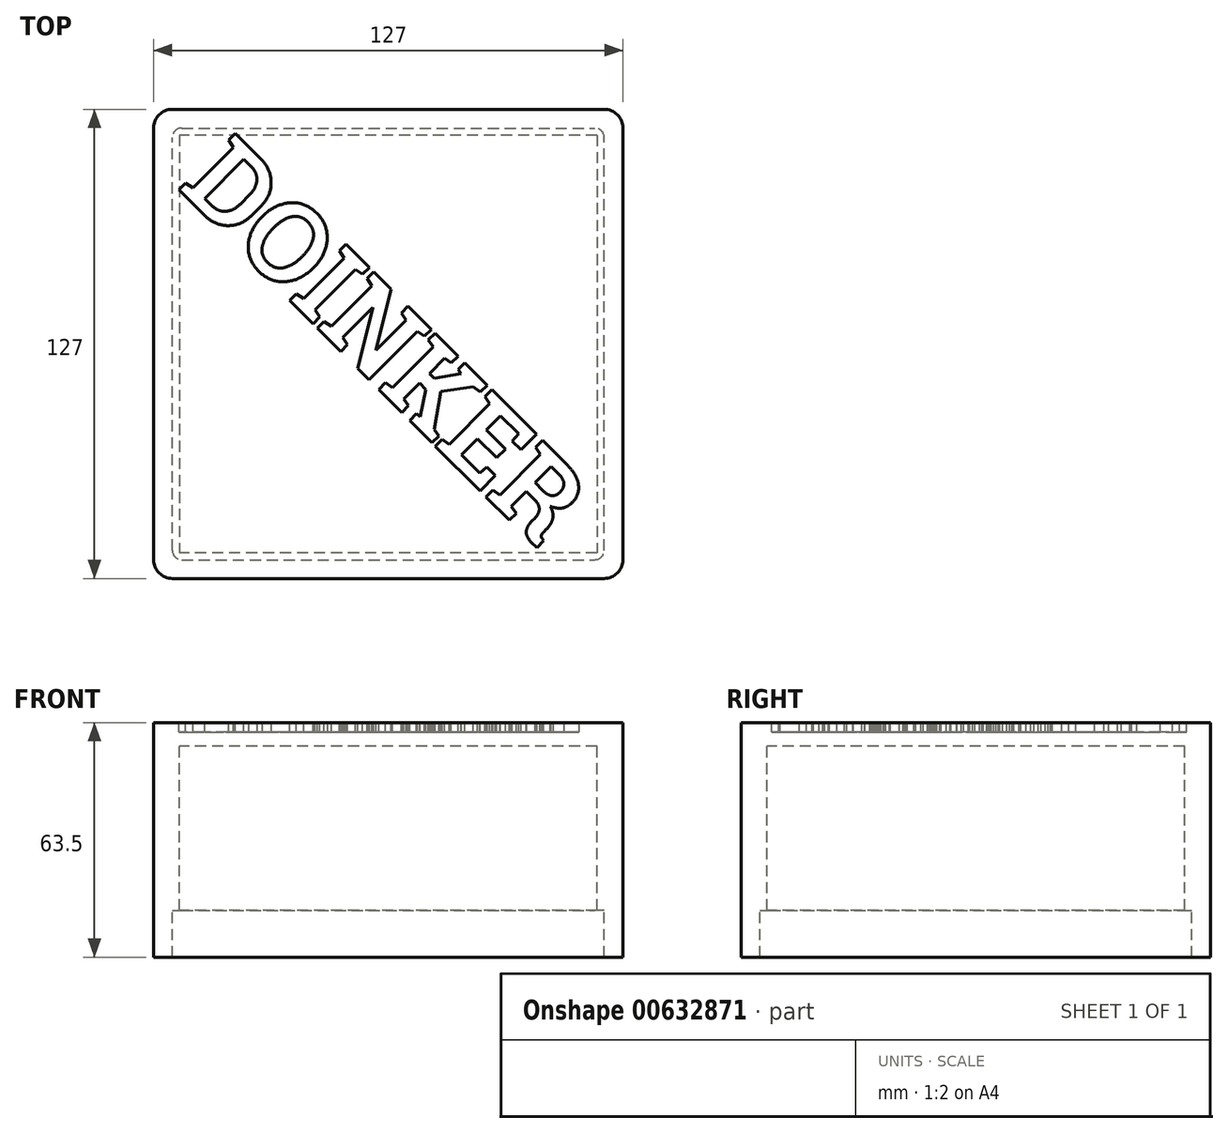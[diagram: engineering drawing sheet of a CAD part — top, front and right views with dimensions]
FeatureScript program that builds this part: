
annotation { "Feature Type Name" : "Feature", "Feature Type Description" : "" }
export const myFeature = defineFeature(function(context is Context, id is Id, definition is map)
    precondition{}
    {
        {
            var Q0;
            Q0=qCreatedBy(makeId("Top.planeOp"),FACE);
            var sketch = newSketch(context, id + "F0", { "sketchPlane" : qUnion([Q0])});
            skLineSegment(sketch, "E0.bottom", {"start": v(56.51, 56.52) * mm, "end": v(-56.52, 56.52) * mm});
            skLineSegment(sketch, "E0.top", {"start": v(56.52, -56.52) * mm, "end": v(-56.51, -56.52) * mm});
            skLineSegment(sketch, "E0.left", {"start": v(56.51, 56.52) * mm, "end": v(56.52, -56.52) * mm});
            skLineSegment(sketch, "E0.right", {"start": v(-56.52, 56.52) * mm, "end": v(-56.51, -56.52) * mm});
            skPoint(sketch, "E0.middle", {"position": v(0, 0) * mm});
            skLineSegment(sketch, "E1.bottom", {"start": v(-63.5, 63.5) * mm, "end": v(63.5, 63.5) * mm});
            skLineSegment(sketch, "E1.top", {"start": v(-63.5, -63.5) * mm, "end": v(63.5, -63.5) * mm});
            skLineSegment(sketch, "E1.left", {"start": v(-63.5, 63.5) * mm, "end": v(-63.5, -63.5) * mm});
            skLineSegment(sketch, "E1.right", {"start": v(63.5, 63.5) * mm, "end": v(63.5, -63.5) * mm});
            skSolve(sketch);
        }
        {
            var Q0;
            Q0=qSketchRegion(id+"F0",true);
            extrude(context, id + "F1", {"entities" : qUnion([Q0]), "oppositeDirection" : true, "depth" : 50.8 * mm, "offsetDistance" : 25.4 * mm});
        }
        {
            var Q0;
            Q0=qCreatedBy(makeId("Top.planeOp"),FACE);
            var sketch = newSketch(context, id + "F2", { "sketchPlane" : qUnion([Q0])});
            skLineSegment(sketch, "E2.bottom", {"start": v(56.51, 56.52) * mm, "end": v(-56.52, 56.52) * mm});
            skLineSegment(sketch, "E2.top", {"start": v(56.52, -56.52) * mm, "end": v(-56.51, -56.52) * mm});
            skLineSegment(sketch, "E2.left", {"start": v(56.51, 56.52) * mm, "end": v(56.52, -56.52) * mm});
            skLineSegment(sketch, "E2.right", {"start": v(-56.52, 56.52) * mm, "end": v(-56.51, -56.52) * mm});
            skPoint(sketch, "E2.middle", {"position": v(0, 0) * mm});
            skSolve(sketch);
        }
        {
            var Q0;
            Q0=makeQuery(id+"F2.imprint","IMPRINT",FACE,{"disambiguationData":[TD([[makeQuery(id+"F2.imprint","IMPRINT",EDGE,{"derivedFrom":sQuery(id+"F2.wireOp",EDGE,"E2.bottom")}),1.0]])]});
            extrude(context, id + "F3", {"entities" : qUnion([Q0]), "operationType" : NewBodyOperationType.ADD, "oppositeDirection" : true, "depth" : 6.35 * mm, "offsetDistance" : 25.4 * mm});
        }
        {
            var Q0;
            Q0=makeQuery(id+"F1.opExtrude","CAP_FACE",FACE,{"disambiguationData":[OSD([sQuery(id+"F0.wireOp",EDGE,"E0.bottom"),sQuery(id+"F0.wireOp",EDGE,"E0.top"),sQuery(id+"F0.wireOp",EDGE,"E0.left"),sQuery(id+"F0.wireOp",EDGE,"E0.right"),sQuery(id+"F0.wireOp",EDGE,"E1.bottom"),sQuery(id+"F0.wireOp",EDGE,"E1.top"),sQuery(id+"F0.wireOp",EDGE,"E1.left"),sQuery(id+"F0.wireOp",EDGE,"E1.right")])],"isStart":false});
            var sketch = newSketch(context, id + "F4", { "sketchPlane" : qUnion([Q0])});
            skLineSegment(sketch, "E3.bottom", {"start": v(-58.42, 58.42) * mm, "end": v(58.42, 58.42) * mm});
            skLineSegment(sketch, "E3.top", {"start": v(-58.42, -58.42) * mm, "end": v(58.42, -58.42) * mm});
            skLineSegment(sketch, "E3.left", {"start": v(-58.42, 58.42) * mm, "end": v(-58.42, -58.42) * mm});
            skLineSegment(sketch, "E3.right", {"start": v(58.42, 58.42) * mm, "end": v(58.42, -58.42) * mm});
            skPoint(sketch, "E3.middle", {"position": v(0, 0) * mm});
            skSolve(sketch);
        }
        {
            var Q0;
            Q0=makeQuery(id+"F4.imprint","IMPRINT",FACE,{"disambiguationData":[TD([[makeQuery(id+"F4.imprint","IMPRINT",EDGE,{"derivedFrom":sQuery(id+"F4.wireOp",EDGE,"E3.bottom")}),1.0]])]});
            extrude(context, id + "F5", {"entities" : qUnion([Q0]), "operationType" : NewBodyOperationType.ADD, "depth" : 12.7 * mm, "offsetDistance" : 25.4 * mm});
        }
        {
            var Q0;
            {var subQ0=sQuery(id+"F0.wireOp",EDGE,"E1.left");var subQ1=sQuery(id+"F0.wireOp",EDGE,"E1.top");Q0=makeQuery(id+"F5.boolean.opBoolean","MERGE",EDGE,{"derivedFrom":[makeQuery(id+"F1.opExtrude","SWEPT_EDGE",EDGE,{"disambiguationData":[OSD([subQ1,subQ0])]}),makeQuery(id+"F5.opExtrude","SWEPT_EDGE",EDGE,{"disambiguationData":[OSD([subQ1,subQ0])]})]});}
            var Q1;
            {var subQ0=sQuery(id+"F0.wireOp",EDGE,"E1.right");var subQ1=sQuery(id+"F0.wireOp",EDGE,"E1.top");Q1=makeQuery(id+"F5.boolean.opBoolean","MERGE",EDGE,{"derivedFrom":[makeQuery(id+"F1.opExtrude","SWEPT_EDGE",EDGE,{"disambiguationData":[OSD([subQ1,subQ0])]}),makeQuery(id+"F5.opExtrude","SWEPT_EDGE",EDGE,{"disambiguationData":[OSD([subQ1,subQ0])]})]});}
            var Q2;
            {var subQ0=sQuery(id+"F0.wireOp",EDGE,"E1.right");var subQ1=sQuery(id+"F0.wireOp",EDGE,"E1.bottom");Q2=makeQuery(id+"F5.boolean.opBoolean","MERGE",EDGE,{"derivedFrom":[makeQuery(id+"F1.opExtrude","SWEPT_EDGE",EDGE,{"disambiguationData":[OSD([subQ1,subQ0])]}),makeQuery(id+"F5.opExtrude","SWEPT_EDGE",EDGE,{"disambiguationData":[OSD([subQ1,subQ0])]})]});}
            var Q3;
            {var subQ0=sQuery(id+"F0.wireOp",EDGE,"E1.left");var subQ1=sQuery(id+"F0.wireOp",EDGE,"E1.bottom");Q3=makeQuery(id+"F5.boolean.opBoolean","MERGE",EDGE,{"derivedFrom":[makeQuery(id+"F1.opExtrude","SWEPT_EDGE",EDGE,{"disambiguationData":[OSD([subQ1,subQ0])]}),makeQuery(id+"F5.opExtrude","SWEPT_EDGE",EDGE,{"disambiguationData":[OSD([subQ1,subQ0])]})]});}
            fillet(context, id + "F6", {"entities" : qUnion([Q0, Q1, Q2, Q3]), "radius" : 5.08 * mm, "tangentPropagation" : true, "allowEdgeOverflow" : false});
        }
        {
            var Q0;
            Q0=makeQuery(id+"F5.opExtrude","SWEPT_EDGE",EDGE,{"disambiguationData":[OSD([sQuery(id+"F4.wireOp",EDGE,"E3.bottom"),sQuery(id+"F4.wireOp",EDGE,"E3.right")])]});
            var Q1;
            Q1=makeQuery(id+"F5.opExtrude","SWEPT_EDGE",EDGE,{"disambiguationData":[OSD([sQuery(id+"F4.wireOp",EDGE,"E3.bottom"),sQuery(id+"F4.wireOp",EDGE,"E3.left")])]});
            var Q2;
            Q2=makeQuery(id+"F5.opExtrude","SWEPT_EDGE",EDGE,{"disambiguationData":[OSD([sQuery(id+"F4.wireOp",EDGE,"E3.top"),sQuery(id+"F4.wireOp",EDGE,"E3.left")])]});
            var Q3;
            Q3=makeQuery(id+"F5.opExtrude","SWEPT_EDGE",EDGE,{"disambiguationData":[OSD([sQuery(id+"F4.wireOp",EDGE,"E3.top"),sQuery(id+"F4.wireOp",EDGE,"E3.right")])]});
            fillet(context, id + "F7", {"entities" : qUnion([Q0, Q1, Q2, Q3]), "radius" : 2.54 * mm, "tangentPropagation" : true, "allowEdgeOverflow" : false});
        }
        {
            var Q0;
            Q0=qCreatedBy(makeId("Top.planeOp"),FACE);
            var sketch = newSketch(context, id + "F8", { "sketchPlane" : qUnion([Q0])});
            skText(sketch, "E4", { "text": "DOINKER", "fontName": "RobotoSlab-Bold.ttf"});
            skLineSegment(sketch, "E5.0", {"start": v(-57.24, 42.29) * mm, "end": v(41.54, -56.5) * mm, "construction": true});
            skLineSegment(sketch, "E5.1", {"start": v(41.54, -56.5) * mm, "end": v(41.54, -56.5) * mm});
            const initialGuessF8  = {"E4": [-0.05724, 0.04229, 0.7071, -0.7071, 0.02187]};
            skSetInitialGuess(sketch, initialGuessF8);
            skSolve(sketch);
        }
        {
            var Q0;
            Q0 = qSketchRegion(id + "F8", true);
            extrude(context, id + "F9", {"entities" : qUnion([Q0]), "operationType" : NewBodyOperationType.REMOVE, "oppositeDirection" : true, "depth" : 2.54 * mm, "offsetDistance" : 25.4 * mm});
        }
    });
